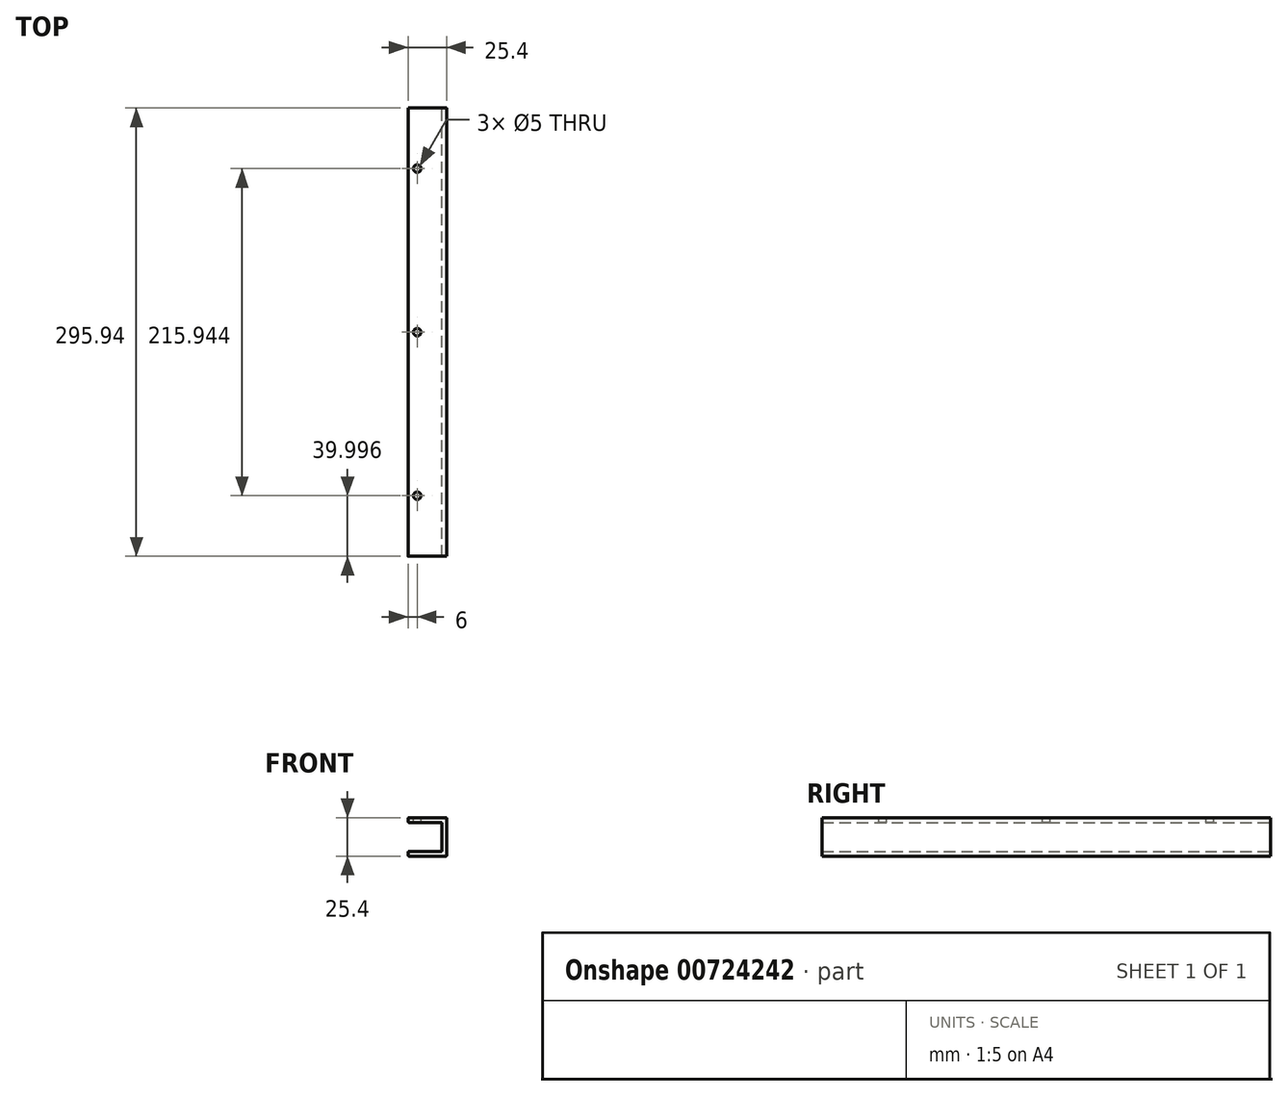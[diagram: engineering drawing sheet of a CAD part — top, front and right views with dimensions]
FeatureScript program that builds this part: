
annotation { "Feature Type Name" : "Feature", "Feature Type Description" : "" }
export const myFeature = defineFeature(function(context is Context, id is Id, definition is map)
    precondition{}
    {
        {
            var Q0;
            Q0=qCreatedBy(makeId("Front.planeOp"),FACE);
            var sketch = newSketch(context, id + "F0", { "sketchPlane" : qUnion([Q0])});
            skLineSegment(sketch, "E0", {"start": v(0, 0) * mm, "end": v(25.4, 0) * mm});
            skLineSegment(sketch, "E1", {"start": v(25.4, 0) * mm, "end": v(25.4, 25.4) * mm});
            skLineSegment(sketch, "E2", {"start": v(25.4, 25.4) * mm, "end": v(0, 25.4) * mm});
            skLineSegment(sketch, "E3", {"start": v(0, 25.4) * mm, "end": v(0, 22.22) * mm});
            skLineSegment(sketch, "E4", {"start": v(0, 22.22) * mm, "end": v(22.4, 22.23) * mm});
            skLineSegment(sketch, "E5", {"start": v(22.4, 22.23) * mm, "end": v(22.4, 3) * mm});
            skLineSegment(sketch, "E6", {"start": v(22.4, 3) * mm, "end": v(0, 3) * mm});
            skLineSegment(sketch, "E7", {"start": v(0, 3) * mm, "end": v(0, 0) * mm});
            skSolve(sketch);
        }
        {
            var Q0;
            Q0=makeQuery(id+"F0.imprint","IMPRINT",FACE,{"disambiguationData":[TD([[makeQuery(id+"F0.imprint","IMPRINT",EDGE,{"derivedFrom":sQuery(id+"F0.wireOp",EDGE,"E0")}),1.0]])]});
            extrude(context, id + "F1", {"entities" : qUnion([Q0]), "depth" : 295.94 * mm, "offsetDistance" : 25 * mm});
        }
        {
            var Q0;
            Q0=makeQuery(id+"F1.opExtrude","SWEPT_FACE",FACE,{"disambiguationData":[OSD([sQuery(id+"F0.wireOp",EDGE,"E2")])]});
            var sketch = newSketch(context, id + "F2", { "sketchPlane" : qUnion([Q0])});
            skCircle(sketch, "E8", {"center": v(6, -40) * mm, "radius": 2.5 * mm});
            skCircle(sketch, "E9", {"center": v(6, -147.97) * mm, "radius": 2.5 * mm});
            skCircle(sketch, "E10", {"center": v(6, -255.94) * mm, "radius": 2.5 * mm});
            skLineSegment(sketch, "E11", {"start": v(6, 0) * mm, "end": v(6, -40) * mm, "construction": true});
            skLineSegment(sketch, "E12", {"start": v(6, -147.97) * mm, "end": v(6, -40) * mm, "construction": true});
            skLineSegment(sketch, "E13", {"start": v(6, -147.97) * mm, "end": v(6, -255.94) * mm, "construction": true});
            skLineSegment(sketch, "E14", {"start": v(6, -255.94) * mm, "end": v(6, -295.94) * mm, "construction": true});
            skSolve(sketch);
        }
        {
            var Q0;
            Q0=qSketchRegion(id+"F2",true);
            extrude(context, id + "F3", {"entities" : qUnion([Q0]), "operationType" : NewBodyOperationType.REMOVE, "oppositeDirection" : true, "depth" : 5 * mm, "offsetDistance" : 25 * mm});
        }
        {
            var Q0;
            Q0=makeQuery(id+"F1.opExtrude","SWEPT_FACE",FACE,{"disambiguationData":[OSD([sQuery(id+"F0.wireOp",EDGE,"E2")])]});
            var sketch = newSketch(context, id + "F4", { "sketchPlane" : qUnion([Q0])});
            skLineSegment(sketch, "E15", {"start": v(25.4, -295.94) * mm, "end": v(25.4, -270.94) * mm});
            skLineSegment(sketch, "E16", {"start": v(25.4, -270.94) * mm, "end": v(0, -295.94) * mm});
            skLineSegment(sketch, "E17", {"start": v(0, -295.94) * mm, "end": v(25.4, -295.94) * mm});
            skSolve(sketch);
        }
        {
            var Q0;
            Q0=makeQuery(id+"F1.opExtrude","SWEPT_EDGE",EDGE,{"disambiguationData":[OSD([sQuery(id+"F0.wireOp",EDGE,"E1"),sQuery(id+"F0.wireOp",EDGE,"E2")])]});
            var Q1;
            Q1=makeQuery(id+"F1.opExtrude","SWEPT_EDGE",EDGE,{"disambiguationData":[OSD([sQuery(id+"F0.wireOp",EDGE,"E0"),sQuery(id+"F0.wireOp",EDGE,"E1")])]});
            var Q2;
            Q2=makeQuery(id+"F1.opExtrude","SWEPT_EDGE",EDGE,{"disambiguationData":[OSD([sQuery(id+"F0.wireOp",EDGE,"E2"),sQuery(id+"F0.wireOp",EDGE,"E3")])]});
            var Q3;
            Q3=makeQuery(id+"F1.opExtrude","SWEPT_EDGE",EDGE,{"disambiguationData":[OSD([sQuery(id+"F0.wireOp",EDGE,"E3"),sQuery(id+"F0.wireOp",EDGE,"E4")])]});
            var Q4;
            Q4=makeQuery(id+"F1.opExtrude","SWEPT_EDGE",EDGE,{"disambiguationData":[OSD([sQuery(id+"F0.wireOp",EDGE,"E4"),sQuery(id+"F0.wireOp",EDGE,"E5")])]});
            var Q5;
            Q5=makeQuery(id+"F1.opExtrude","SWEPT_EDGE",EDGE,{"disambiguationData":[OSD([sQuery(id+"F0.wireOp",EDGE,"E6"),sQuery(id+"F0.wireOp",EDGE,"E7")])]});
            var Q6;
            Q6=makeQuery(id+"F1.opExtrude","SWEPT_EDGE",EDGE,{"disambiguationData":[OSD([sQuery(id+"F0.wireOp",EDGE,"E0"),sQuery(id+"F0.wireOp",EDGE,"E7")])]});
            var Q7;
            Q7=makeQuery(id+"F1.opExtrude","SWEPT_EDGE",EDGE,{"disambiguationData":[OSD([sQuery(id+"F0.wireOp",EDGE,"E5"),sQuery(id+"F0.wireOp",EDGE,"E6")])]});
            fillet(context, id + "F5", {"entities" : qUnion([Q0, Q1, Q2, Q3, Q4, Q5, Q6, Q7]), "radius" : 0.5 * mm, "tangentPropagation" : true, "allowEdgeOverflow" : false});
        }
    });
